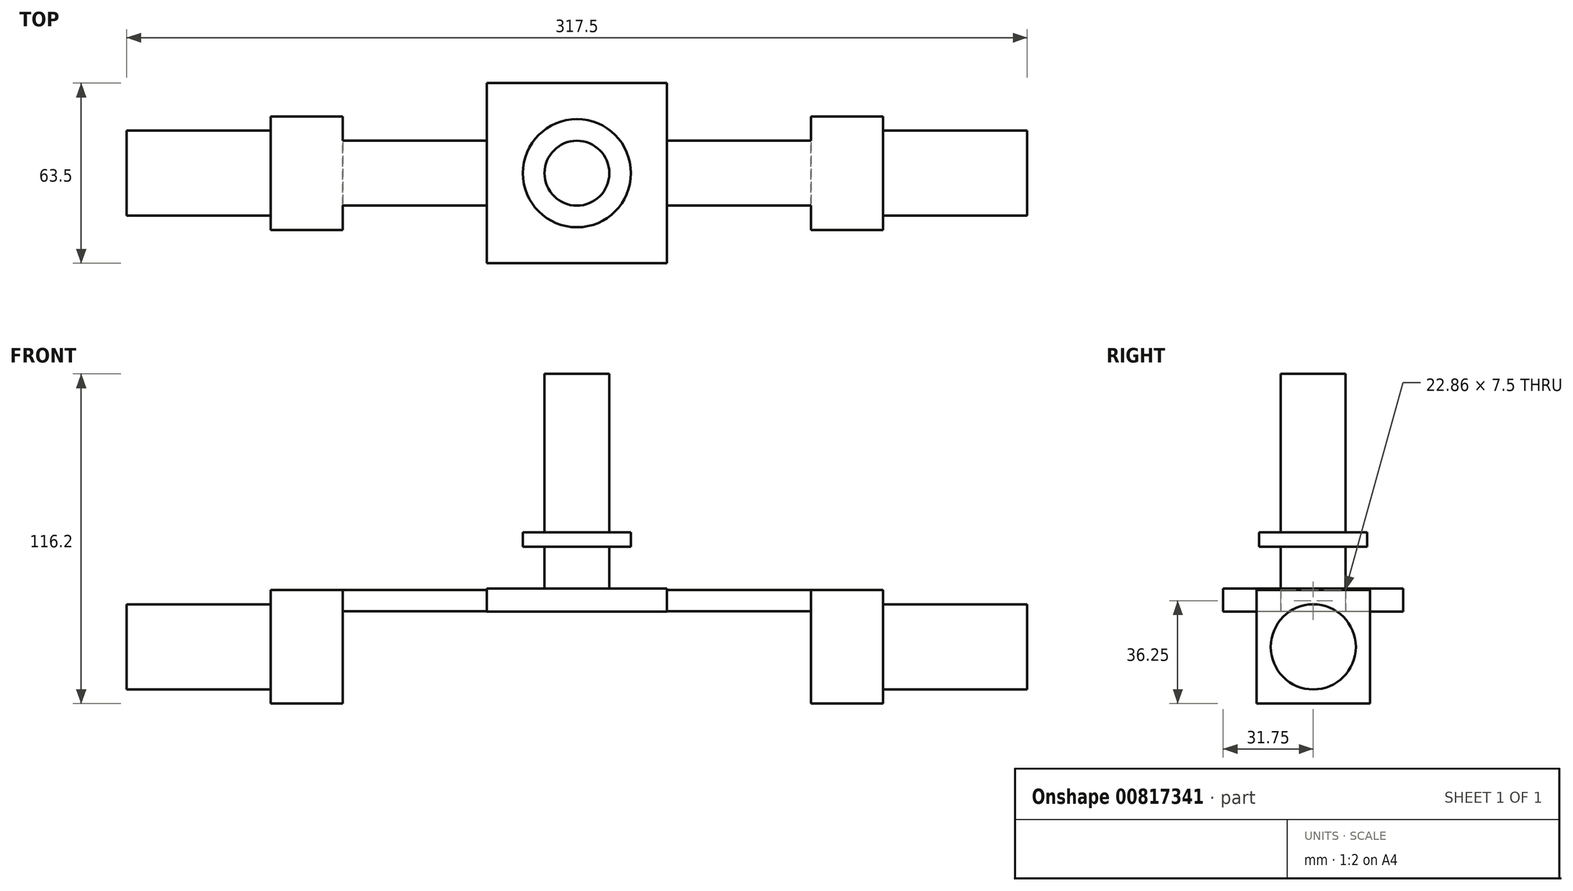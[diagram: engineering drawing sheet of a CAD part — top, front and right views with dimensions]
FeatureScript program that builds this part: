
annotation { "Feature Type Name" : "Feature", "Feature Type Description" : "" }
export const myFeature = defineFeature(function(context is Context, id is Id, definition is map)
    precondition{}
    {
        {
            var Q0;
            Q0=qCreatedBy(makeId("Top.planeOp"),FACE);
            var sketch = newSketch(context, id + "F0", { "sketchPlane" : qUnion([Q0])});
            skCircle(sketch, "E0", {"center": v(0, 0) * mm, "radius": 11.43 * mm});
            skSolve(sketch);
        }
        {
            var Q0;
            Q0=makeQuery(id+"F0.imprint","IMPRINT",FACE,{"disambiguationData":[TD([[makeQuery(id+"F0.imprint","IMPRINT",EDGE,{"derivedFrom":sQuery(id+"F0.wireOp",EDGE,"E0")}),1.0]])]});
            extrude(context, id + "F1", {"entities" : qUnion([Q0]), "depth" : 76.2 * mm, "offsetDistance" : 25.4 * mm});
        }
        {
            var Q0;
            Q0=qCreatedBy(makeId("Top.planeOp"),FACE);
            var sketch = newSketch(context, id + "F2", { "sketchPlane" : qUnion([Q0])});
            skCircle(sketch, "E1", {"center": v(0, 0) * mm, "radius": 19.05 * mm});
            skCircle(sketch, "E2", {"center": v(0, 0) * mm, "radius": 22.23 * mm});
            skLineSegment(sketch, "E3.bottom", {"start": v(31.75, 31.75) * mm, "end": v(-31.75, 31.75) * mm});
            skLineSegment(sketch, "E3.top", {"start": v(31.75, -31.75) * mm, "end": v(-31.75, -31.75) * mm});
            skLineSegment(sketch, "E3.left", {"start": v(31.75, 31.75) * mm, "end": v(31.75, -31.75) * mm});
            skLineSegment(sketch, "E3.right", {"start": v(-31.75, 31.75) * mm, "end": v(-31.75, -31.75) * mm});
            skSolve(sketch);
        }
        {
            var Q0;
            Q0=makeQuery(id+"F2.imprint","IMPRINT",FACE,{"disambiguationData":[TD([[makeQuery(id+"F2.imprint","IMPRINT",EDGE,{"derivedFrom":sQuery(id+"F2.wireOp",EDGE,"E1")}),1.0]])]});
            extrude(context, id + "F3", {"entities" : qUnion([Q0]), "operationType" : NewBodyOperationType.ADD, "depth" : 20.32 * mm, "offsetDistance" : 25.4 * mm, "hasSecondDirection" : true, "secondDirectionOppositeDirection" : false, "secondDirectionDepth" : 15.24 * mm});
        }
        {
            var Q0;
            Q0=qCreatedBy(makeId("Top.planeOp"),FACE);
            var sketch = newSketch(context, id + "F4", { "sketchPlane" : qUnion([Q0])});
            skLineSegment(sketch, "E4.bottom", {"start": v(107.95, -11.43) * mm, "end": v(-107.95, -11.43) * mm});
            skLineSegment(sketch, "E4.top", {"start": v(107.95, 11.43) * mm, "end": v(-107.95, 11.43) * mm});
            skLineSegment(sketch, "E4.left", {"start": v(107.95, -11.43) * mm, "end": v(107.95, 11.43) * mm});
            skLineSegment(sketch, "E4.right", {"start": v(-107.95, -11.43) * mm, "end": v(-107.95, 11.43) * mm});
            skPoint(sketch, "E4.middle", {"position": v(0, 0) * mm});
            skCircle(sketch, "E5", {"center": v(-97.8, 0) * mm, "radius": 5.08 * mm});
            skCircle(sketch, "E6", {"center": v(97.8, 0) * mm, "radius": 5.08 * mm});
            skSolve(sketch);
        }
        {
            var Q0;
            Q0=makeQuery(id+"F4.imprint","IMPRINT",FACE,{"disambiguationData":[TD([[makeQuery(id+"F4.imprint","IMPRINT",EDGE,{"derivedFrom":sQuery(id+"F4.wireOp",EDGE,"E4.bottom")}),-1.0]])]});
            extrude(context, id + "F5", {"entities" : qUnion([Q0]), "operationType" : NewBodyOperationType.ADD, "oppositeDirection" : true, "depth" : 7.5 * mm, "offsetDistance" : 25.4 * mm});
        }
        {
            var Q0;
            Q0 = qSketchRegion(id + "F2", true);
            var Q1;
            Q1=makeQuery(id+"F2.imprint","IMPRINT",FACE,{"disambiguationData":[TD([[makeQuery(id+"F2.imprint","IMPRINT",EDGE,{"derivedFrom":sQuery(id+"F2.wireOp",EDGE,"E1")}),1.0]])]});
            var Q2;
            Q2=makeQuery(id+"F2.imprint","IMPRINT",FACE,{"disambiguationData":[TD([[makeQuery(id+"F2.imprint","IMPRINT",EDGE,{"derivedFrom":sQuery(id+"F2.wireOp",EDGE,"E1")}),-1.0]])]});
            extrude(context, id + "F6", {"entities" : qUnion([Q0, Q1, Q2]), "operationType" : NewBodyOperationType.ADD, "depth" : 0.5 * mm, "offsetDistance" : 25.4 * mm, "hasSecondDirection" : true, "secondDirectionOppositeDirection" : true, "secondDirectionDepth" : 7.62 * mm});
        }
        {
            var Q0;
            Q0=qCreatedBy(makeId("Right.planeOp"),FACE);
            var sketch = newSketch(context, id + "F7", { "sketchPlane" : qUnion([Q0])});
            skLineSegment(sketch, "E7.bottom", {"start": v(20, 0) * mm, "end": v(-20, 0) * mm});
            skLineSegment(sketch, "E7.top", {"start": v(20, -40) * mm, "end": v(-20, -40) * mm});
            skLineSegment(sketch, "E7.left", {"start": v(20, 0) * mm, "end": v(20, -40) * mm});
            skLineSegment(sketch, "E7.right", {"start": v(-20, 0) * mm, "end": v(-20, -40) * mm});
            skPoint(sketch, "E7.middle", {"position": v(0, -20) * mm});
            skCircle(sketch, "E8", {"center": v(0, -20) * mm, "radius": 15 * mm});
            skSolve(sketch);
        }
        {
            var Q0;
            Q0 = qSketchRegion(id + "F7", true);
            var Q1;
            Q1=makeQuery(id+"F7.imprint","IMPRINT",FACE,{"disambiguationData":[TD([[makeQuery(id+"F7.imprint","IMPRINT",EDGE,{"derivedFrom":sQuery(id+"F7.wireOp",EDGE,"E8")}),1.0]])]});
            extrude(context, id + "F8", {"entities" : qUnion([Q0, Q1]), "operationType" : NewBodyOperationType.ADD, "depth" : 107.95 * mm, "offsetDistance" : 25.4 * mm, "hasSecondDirection" : true, "secondDirectionOppositeDirection" : false, "secondDirectionDepth" : 82.55 * mm});
        }
        {
            var Q0;
            Q0=makeQuery(id+"F7.imprint","IMPRINT",FACE,{"disambiguationData":[TD([[makeQuery(id+"F7.imprint","IMPRINT",EDGE,{"derivedFrom":sQuery(id+"F7.wireOp",EDGE,"E8")}),1.0]])]});
            extrude(context, id + "F9", {"entities" : qUnion([Q0]), "operationType" : NewBodyOperationType.ADD, "depth" : 158.75 * mm, "offsetDistance" : 25.4 * mm, "hasSecondDirection" : true, "secondDirectionOppositeDirection" : false, "secondDirectionDepth" : 107.95 * mm});
        }
        {
            var Q0;
            Q0=makeQuery(id+"F7.imprint","IMPRINT",FACE,{"disambiguationData":[TD([[makeQuery(id+"F7.imprint","IMPRINT",EDGE,{"derivedFrom":sQuery(id+"F7.wireOp",EDGE,"E7.bottom")}),1.0]])]});
            var Q1;
            Q1=makeQuery(id+"F7.imprint","IMPRINT",FACE,{"disambiguationData":[TD([[makeQuery(id+"F7.imprint","IMPRINT",EDGE,{"derivedFrom":sQuery(id+"F7.wireOp",EDGE,"E8")}),1.0]])]});
            extrude(context, id + "F10", {"entities" : qUnion([Q0, Q1]), "operationType" : NewBodyOperationType.ADD, "oppositeDirection" : true, "depth" : 107.95 * mm, "offsetDistance" : 25.4 * mm, "hasSecondDirection" : true, "secondDirectionOppositeDirection" : true, "secondDirectionDepth" : 82.55 * mm});
        }
        {
            var Q0;
            Q0=makeQuery(id+"F7.imprint","IMPRINT",FACE,{"disambiguationData":[TD([[makeQuery(id+"F7.imprint","IMPRINT",EDGE,{"derivedFrom":sQuery(id+"F7.wireOp",EDGE,"E8")}),1.0]])]});
            extrude(context, id + "F11", {"entities" : qUnion([Q0]), "operationType" : NewBodyOperationType.ADD, "oppositeDirection" : true, "depth" : 158.75 * mm, "offsetDistance" : 25.4 * mm, "hasSecondDirection" : true, "secondDirectionOppositeDirection" : true, "secondDirectionDepth" : 107.95 * mm});
        }
    });
